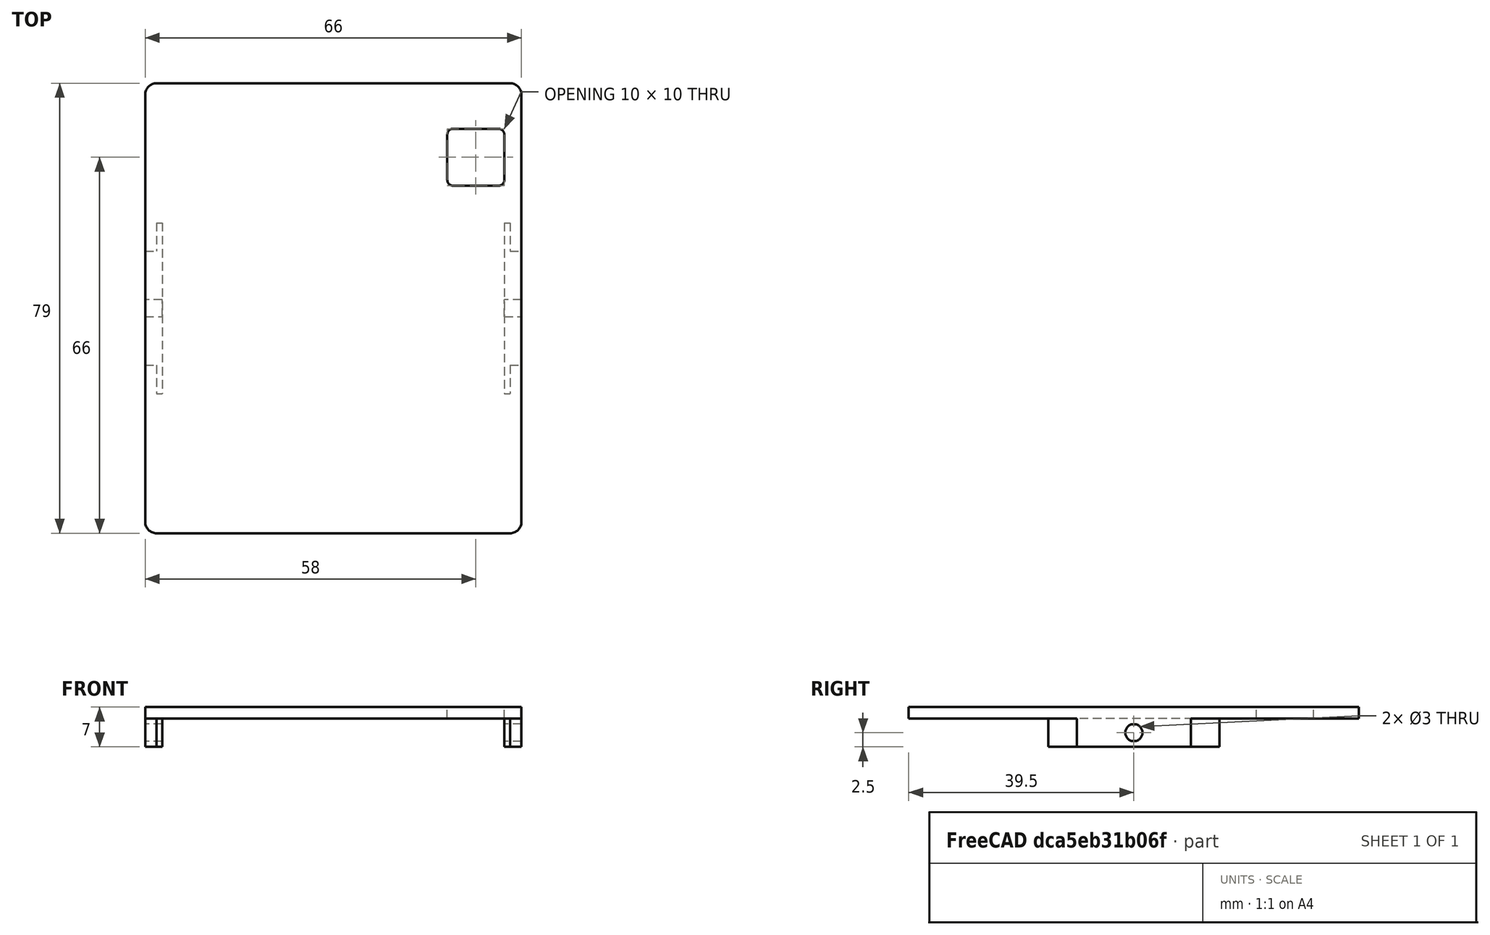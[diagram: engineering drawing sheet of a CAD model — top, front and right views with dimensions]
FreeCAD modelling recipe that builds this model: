
FCSTD DOCUMENT  (FreeCAD 0.21R33771 (Git))
Label: controlbox-top
License: All rights reserved
LicenseURL: http://en.wikipedia.org/wiki/All_rights_reserved
objects: PartDesign::AdditiveBox×3, PartDesign::LinearPattern×3, PartDesign::Fillet×2, PartDesign::SubtractiveBox×1, PartDesign::SubtractiveCylinder×1, PartDesign::Body×1
note: 18 computed .brp shape members not serialized (recipe doc carries the construction recipe); baked Part::Feature solids carry a one-line shape summary decoded from their .brp

FEATURE [PartDesign::AdditiveBox] Box
  AttacherType = Attacher::AttachEngine3D
  Height = 2
  Length = 66
  Width = 79
FEATURE [PartDesign::Fillet] Fillet
  Base = -> Box [Edge1,Edge5,Edge7,Edge3]
  BaseFeature = -> Box
  Radius = 2
  SupportTransform = false
  UseAllEdges = false
FEATURE [PartDesign::SubtractiveBox] Box001
  AttacherType = Attacher::AttachEngine3D
  AttachmentOffset = pos=(53,61,-2) rot=(0,0,1;0rad)
  BaseFeature = -> Fillet
  Height = 2
  Length = 10
  MapMode = 5
  Placement = pos=(53,61,0) rot=(0,0,1;0rad)
  Support = -> [Fillet]
  Width = 10
FEATURE [PartDesign::Fillet] Fillet001
  Base = -> Box001 [Edge34,Edge36,Edge33,Edge35]
  BaseFeature = -> Box001
  Placement = pos=(53,61,0) rot=(0,0,1;0rad)
  Radius = 1
  SupportTransform = false
  UseAllEdges = false
FEATURE [PartDesign::AdditiveBox] Box002
  AttacherType = Attacher::AttachEngine3D
  AttachmentOffset = pos=(11,11.5,0) rot=(0,0,1;0rad)
  BaseFeature = -> Fillet001
  Height = 5
  Length = 2
  MapMode = 5
  Placement = pos=(64,49.5,0) rot=(1,0,0;3.14159rad)
  Support = -> [Fillet001]
  Width = 20
FEATURE [PartDesign::LinearPattern] LinearPattern
  BaseFeature = -> Box002
  Direction = -> X_Axis
  Length = 64
  Occurrences = 2
  Originals = -> [Box002]
  Placement = pos=(64,49.5,0) rot=(1,0,0;3.14159rad)
  Reversed = true
FEATURE [PartDesign::AdditiveBox] Box003
  AttacherType = Attacher::AttachEngine3D
  AttachmentOffset = pos=(-1,-5,0) rot=(0,0,1;0rad)
  BaseFeature = -> LinearPattern
  Height = 5
  Length = 1
  MapMode = 5
  Placement = pos=(63,54.5,6e-16) rot=(1,0,0;3.14159rad)
  Support = -> [LinearPattern]
  Width = 30
FEATURE [PartDesign::LinearPattern] LinearPattern001
  BaseFeature = -> Box003
  Direction = -> X_Axis
  Length = 61
  Occurrences = 2
  Originals = -> [Box003]
  Placement = pos=(63,54.5,6e-16) rot=(1,0,0;3.14159rad)
  Reversed = true
FEATURE [PartDesign::SubtractiveCylinder] Cylinder
  Angle = 360
  AttacherType = Attacher::AttachEngine3D
  AttachmentOffset = pos=(15,2.5,-3) rot=(0,0,1;0rad)
  BaseFeature = -> LinearPattern001
  FirstAngle = 0
  Height = 3
  MapMode = 5
  Placement = pos=(63,39.5,-2.5) rot=(-0.57735,0.57735,-0.57735;2.0944rad)
  Radius = 1.5
  SecondAngle = 0
  Support = -> [LinearPattern001]
FEATURE [PartDesign::LinearPattern] LinearPattern002
  BaseFeature = -> Cylinder
  Direction = -> X_Axis
  Length = 63
  Occurrences = 2
  Originals = -> [Cylinder]
  Placement = pos=(63,39.5,-2.5) rot=(-0.57735,0.57735,-0.57735;2.0944rad)
  Reversed = true
FEATURE [PartDesign::Body] Body
  Group = -> [Box,Fillet,Box001,Fillet001,Box002,LinearPattern,Box003,LinearPattern001,Cylinder,LinearPattern002]
  Origin = -> Origin
  Tip = -> LinearPattern002
